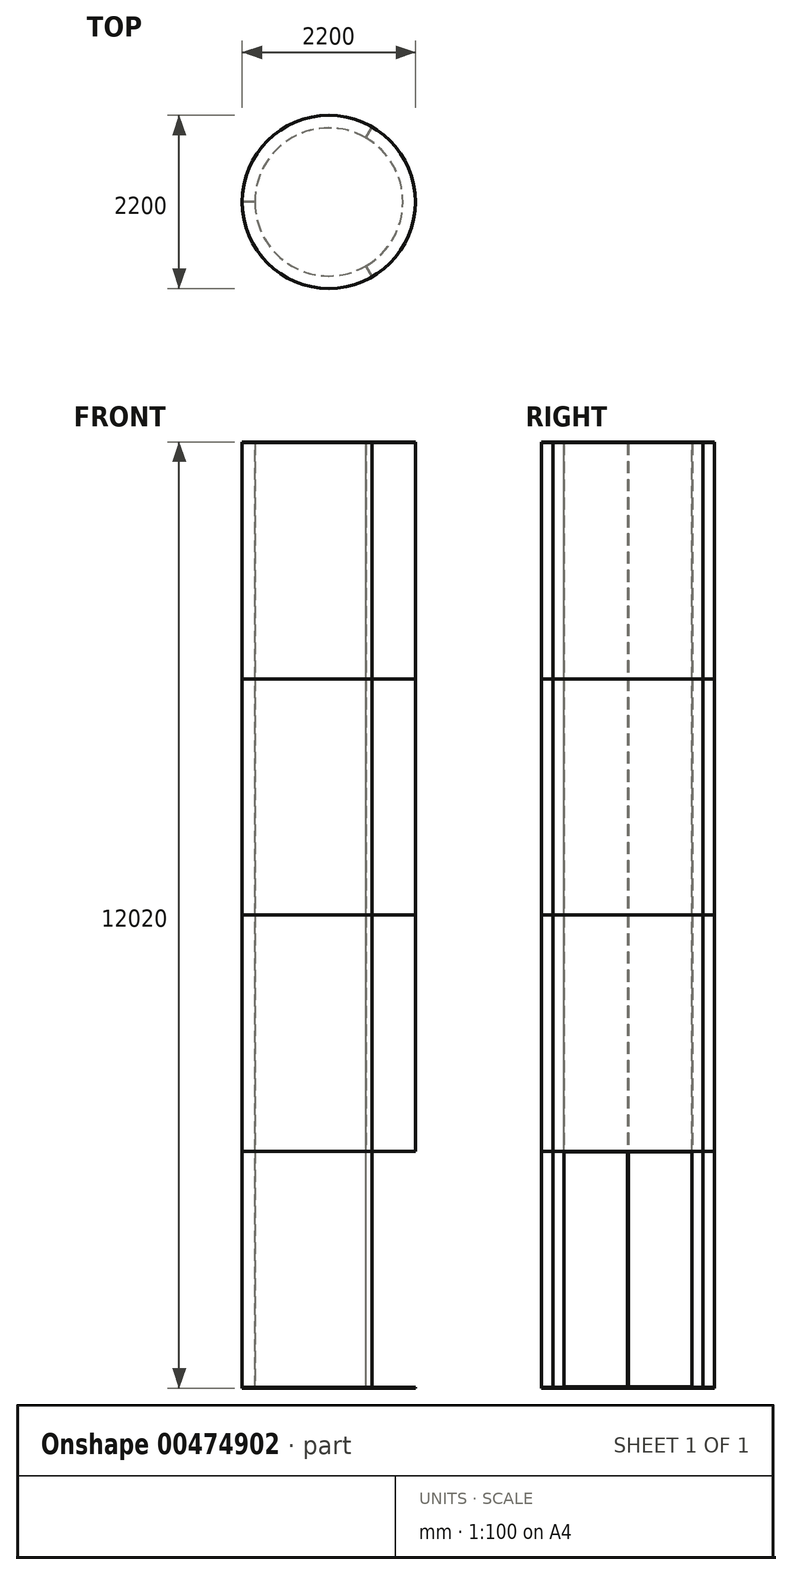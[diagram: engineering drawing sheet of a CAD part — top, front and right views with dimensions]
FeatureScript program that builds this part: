
annotation { "Feature Type Name" : "Feature", "Feature Type Description" : "" }
export const myFeature = defineFeature(function(context is Context, id is Id, definition is map)
    precondition{}
    {
        {
            var Q0;
            Q0=qCreatedBy(makeId("Front.planeOp"),FACE);
            var sketch = newSketch(context, id + "F0", { "sketchPlane" : qUnion([Q0])});
            skLineSegment(sketch, "E0", {"start": v(-940, 1500) * mm, "end": v(-1100, 1500) * mm});
            skLineSegment(sketch, "E1", {"start": v(-1100, 1500) * mm, "end": v(-1100, -1500) * mm});
            skLineSegment(sketch, "E2", {"start": v(-1100, -1500) * mm, "end": v(-940, -1500) * mm});
            skLineSegment(sketch, "E3.0", {"start": v(-1094, -1494) * mm, "end": v(-940, -1494) * mm});
            skLineSegment(sketch, "E3.1", {"start": v(-1094, 1494) * mm, "end": v(-1094, -1494) * mm});
            skLineSegment(sketch, "E3.2", {"start": v(-940, 1494) * mm, "end": v(-1094, 1494) * mm});
            skLineSegment(sketch, "E4", {"start": v(-940, 1494) * mm, "end": v(-940, 1500) * mm});
            skLineSegment(sketch, "E5", {"start": v(-940, -1500) * mm, "end": v(-940, -1494) * mm});
            skLineSegment(sketch, "E6", {"start": v(0, 0) * mm, "end": v(0, 1375.07) * mm, "construction": true});
            skSolve(sketch);
        }
        {
            var Q0;
            Q0 = qSketchRegion(id + "F0", true);
            var Q1;
            Q1=sQuery(id+"F0.wireOp",EDGE,"E6");
            revolve(context, id + "F1", {"entities" : qUnion([Q0]), "axis" : qUnion([Q1]), "revolveType" : RevolveType.TWO_DIRECTIONS, "angle" : 0 * degree, "angleBack" : 240 * degree});
        }
        {
            var Q0;
            Q0=makeQuery(id+"F1.opRevolve","SWEPT_FACE",FACE,{"disambiguationData":[OSD([sQuery(id+"F0.wireOp",EDGE,"E3.0")])]});
            var sketch = newSketch(context, id + "F2", { "sketchPlane" : qUnion([Q0])});
            skLineSegment(sketch, "E7", {"start": v(-940, 0) * mm, "end": v(-1094, 0) * mm});
            skLineSegment(sketch, "E8.0", {"start": v(-939.98, 6) * mm, "end": v(-1093.98, 6) * mm});
            skArc(sketch, "E9", {"start": v(-939.98, 6) * mm, "mid": v(-940, 3) * mm, "end": v(-940, 0) * mm});
            skArc(sketch, "E10", {"start": v(-1093.98, 6) * mm, "mid": v(-1094, 3) * mm, "end": v(-1094, 0) * mm});
            skLineSegment(sketch, "E11", {"start": v(470, 814.06) * mm, "end": v(547, 947.43) * mm});
            skLineSegment(sketch, "E12.0", {"start": v(464.8, 817.05) * mm, "end": v(541.8, 950.42) * mm});
            skArc(sketch, "E13", {"start": v(547, 947.43) * mm, "mid": v(544.4, 948.93) * mm, "end": v(541.8, 950.42) * mm});
            skArc(sketch, "E14", {"start": v(470, 814.06) * mm, "mid": v(467.4, 815.56) * mm, "end": v(464.8, 817.05) * mm});
            skSolve(sketch);
        }
        {
            var Q0;
            Q0=makeQuery(id+"F2.imprint","IMPRINT",FACE,{"disambiguationData":[TD([[makeQuery(id+"F2.imprint","IMPRINT",EDGE,{"derivedFrom":sQuery(id+"F2.wireOp",EDGE,"E7")}),1.0]])]});
            var Q1;
            Q1=makeQuery(id+"F2.imprint","IMPRINT",FACE,{"disambiguationData":[TD([[makeQuery(id+"F2.imprint","IMPRINT",EDGE,{"derivedFrom":sQuery(id+"F2.wireOp",EDGE,"E11")}),-1.0]])]});
            extrude(context, id + "F3", {"entities" : qUnion([Q0, Q1]), "operationType" : NewBodyOperationType.ADD, "depth" : (3000 - 12) * mm});
        }
        {
            var Q0;
            Q0=makeQuery(id+"F1.opRevolve","SWEPT_BODY",BODY,{"disambiguationData":[OSD([sQuery(id+"F0.wireOp",EDGE,"E0"),sQuery(id+"F0.wireOp",EDGE,"E1"),sQuery(id+"F0.wireOp",EDGE,"E2"),sQuery(id+"F0.wireOp",EDGE,"E3.0"),sQuery(id+"F0.wireOp",EDGE,"E3.1"),sQuery(id+"F0.wireOp",EDGE,"E3.2"),sQuery(id+"F0.wireOp",EDGE,"E4"),sQuery(id+"F0.wireOp",EDGE,"E5")])]});
            transform(context, id + "F4", {"entities" : qUnion([Q0]), "transformType" : TransformType.TRANSLATION_3D, "dx" : 0 * mm, "dy" : 0 * mm, "dz" : 3000 * mm, "makeCopy" : true});
        }
        {
            var Q0;
            Q0=makeQuery(id+"F4.opPattern","COPY",BODY,{"derivedFrom":makeQuery(id+"F1.opRevolve","SWEPT_BODY",BODY,{"disambiguationData":[OSD([sQuery(id+"F0.wireOp",EDGE,"E0"),sQuery(id+"F0.wireOp",EDGE,"E1"),sQuery(id+"F0.wireOp",EDGE,"E2"),sQuery(id+"F0.wireOp",EDGE,"E3.0"),sQuery(id+"F0.wireOp",EDGE,"E3.1"),sQuery(id+"F0.wireOp",EDGE,"E3.2"),sQuery(id+"F0.wireOp",EDGE,"E4"),sQuery(id+"F0.wireOp",EDGE,"E5")])]}),"instanceName":"1"});
            deleteBodies(context, id + "F5", {"entities" : qUnion([Q0])});
        }
        {
            var Q0;
            Q0=makeQuery(id+"F1.opRevolve","SWEPT_BODY",BODY,{"disambiguationData":[OSD([sQuery(id+"F0.wireOp",EDGE,"E0"),sQuery(id+"F0.wireOp",EDGE,"E1"),sQuery(id+"F0.wireOp",EDGE,"E2"),sQuery(id+"F0.wireOp",EDGE,"E3.0"),sQuery(id+"F0.wireOp",EDGE,"E3.1"),sQuery(id+"F0.wireOp",EDGE,"E3.2"),sQuery(id+"F0.wireOp",EDGE,"E4"),sQuery(id+"F0.wireOp",EDGE,"E5")])]});
            var Q1;
            Q1=sQuery(id+"F0.wireOp",EDGE,"E6");
            circularPattern(context, id + "F6", {"entities" : qUnion([Q0]), "axis" : qUnion([Q1]), "angle" : 120 * degree, "instanceCount" : 3, "equalSpace" : true, "isCentered" : true});
        }
        {
            var Q0;
            Q0=makeQuery(id+"F6.opPattern","COPY",BODY,{"derivedFrom":makeQuery(id+"F1.opRevolve","SWEPT_BODY",BODY,{"disambiguationData":[OSD([sQuery(id+"F0.wireOp",EDGE,"E0"),sQuery(id+"F0.wireOp",EDGE,"E1"),sQuery(id+"F0.wireOp",EDGE,"E2"),sQuery(id+"F0.wireOp",EDGE,"E3.0"),sQuery(id+"F0.wireOp",EDGE,"E3.1"),sQuery(id+"F0.wireOp",EDGE,"E3.2"),sQuery(id+"F0.wireOp",EDGE,"E4"),sQuery(id+"F0.wireOp",EDGE,"E5")])]}),"instanceName":"-2"});
            deleteBodies(context, id + "F7", {"entities" : qUnion([Q0])});
        }
        {
            var Q0;
            Q0=makeQuery(id+"F6.opPattern","COPY",BODY,{"derivedFrom":makeQuery(id+"F1.opRevolve","SWEPT_BODY",BODY,{"disambiguationData":[OSD([sQuery(id+"F0.wireOp",EDGE,"E0"),sQuery(id+"F0.wireOp",EDGE,"E1"),sQuery(id+"F0.wireOp",EDGE,"E2"),sQuery(id+"F0.wireOp",EDGE,"E3.0"),sQuery(id+"F0.wireOp",EDGE,"E3.1"),sQuery(id+"F0.wireOp",EDGE,"E3.2"),sQuery(id+"F0.wireOp",EDGE,"E4"),sQuery(id+"F0.wireOp",EDGE,"E5")])]}),"instanceName":"1"});
            deleteBodies(context, id + "F8", {"entities" : qUnion([Q0])});
        }
        {
            var Q0;
            Q0=makeQuery(id+"F6.opPattern","COPY",BODY,{"derivedFrom":makeQuery(id+"F1.opRevolve","SWEPT_BODY",BODY,{"disambiguationData":[OSD([sQuery(id+"F0.wireOp",EDGE,"E0"),sQuery(id+"F0.wireOp",EDGE,"E1"),sQuery(id+"F0.wireOp",EDGE,"E2"),sQuery(id+"F0.wireOp",EDGE,"E3.0"),sQuery(id+"F0.wireOp",EDGE,"E3.1"),sQuery(id+"F0.wireOp",EDGE,"E3.2"),sQuery(id+"F0.wireOp",EDGE,"E4"),sQuery(id+"F0.wireOp",EDGE,"E5")])]}),"instanceName":"-1"});
            deleteBodies(context, id + "F9", {"entities" : qUnion([Q0])});
        }
        {
            var Q0;
            Q0=makeQuery(id+"F1.opRevolve","SWEPT_BODY",BODY,{"disambiguationData":[OSD([sQuery(id+"F0.wireOp",EDGE,"E0"),sQuery(id+"F0.wireOp",EDGE,"E1"),sQuery(id+"F0.wireOp",EDGE,"E2"),sQuery(id+"F0.wireOp",EDGE,"E3.0"),sQuery(id+"F0.wireOp",EDGE,"E3.1"),sQuery(id+"F0.wireOp",EDGE,"E3.2"),sQuery(id+"F0.wireOp",EDGE,"E4"),sQuery(id+"F0.wireOp",EDGE,"E5")])]});
            transform(context, id + "F10", {"entities" : qUnion([Q0]), "transformType" : TransformType.TRANSLATION_3D, "dx" : 0 * mm, "dy" : 0 * mm, "dz" : 3000 * mm, "makeCopy" : true});
        }
        {
            var Q0;
            Q0=makeQuery(id+"F10.opPattern","COPY",BODY,{"derivedFrom":makeQuery(id+"F1.opRevolve","SWEPT_BODY",BODY,{"disambiguationData":[OSD([sQuery(id+"F0.wireOp",EDGE,"E0"),sQuery(id+"F0.wireOp",EDGE,"E1"),sQuery(id+"F0.wireOp",EDGE,"E2"),sQuery(id+"F0.wireOp",EDGE,"E3.0"),sQuery(id+"F0.wireOp",EDGE,"E3.1"),sQuery(id+"F0.wireOp",EDGE,"E3.2"),sQuery(id+"F0.wireOp",EDGE,"E4"),sQuery(id+"F0.wireOp",EDGE,"E5")])]}),"instanceName":"1"});
            transform(context, id + "F11", {"entities" : qUnion([Q0]), "transformType" : TransformType.TRANSLATION_3D, "dx" : 0 * mm, "dy" : 0 * mm, "dz" : 3000 * mm, "makeCopy" : true});
        }
        {
            var Q0;
            Q0=makeQuery(id+"F11.opPattern","COPY",BODY,{"derivedFrom":makeQuery(id+"F10.opPattern","COPY",BODY,{"derivedFrom":makeQuery(id+"F1.opRevolve","SWEPT_BODY",BODY,{"disambiguationData":[OSD([sQuery(id+"F0.wireOp",EDGE,"E0"),sQuery(id+"F0.wireOp",EDGE,"E1"),sQuery(id+"F0.wireOp",EDGE,"E2"),sQuery(id+"F0.wireOp",EDGE,"E3.0"),sQuery(id+"F0.wireOp",EDGE,"E3.1"),sQuery(id+"F0.wireOp",EDGE,"E3.2"),sQuery(id+"F0.wireOp",EDGE,"E4"),sQuery(id+"F0.wireOp",EDGE,"E5")])]}),"instanceName":"1"}),"instanceName":"1"});
            transform(context, id + "F12", {"entities" : qUnion([Q0]), "transformType" : TransformType.TRANSLATION_3D, "dx" : 0 * mm, "dy" : 0 * mm, "dz" : 3000 * mm, "makeCopy" : true});
        }
        {
            var Q0;
            Q0=makeQuery(id+"F12.opPattern","COPY",BODY,{"derivedFrom":makeQuery(id+"F11.opPattern","COPY",BODY,{"derivedFrom":makeQuery(id+"F10.opPattern","COPY",BODY,{"derivedFrom":makeQuery(id+"F1.opRevolve","SWEPT_BODY",BODY,{"disambiguationData":[OSD([sQuery(id+"F0.wireOp",EDGE,"E0"),sQuery(id+"F0.wireOp",EDGE,"E1"),sQuery(id+"F0.wireOp",EDGE,"E2"),sQuery(id+"F0.wireOp",EDGE,"E3.0"),sQuery(id+"F0.wireOp",EDGE,"E3.1"),sQuery(id+"F0.wireOp",EDGE,"E3.2"),sQuery(id+"F0.wireOp",EDGE,"E4"),sQuery(id+"F0.wireOp",EDGE,"E5")])]}),"instanceName":"1"}),"instanceName":"1"}),"instanceName":"1"});
            var Q1;
            Q1=makeQuery(id+"F11.opPattern","COPY",BODY,{"derivedFrom":makeQuery(id+"F10.opPattern","COPY",BODY,{"derivedFrom":makeQuery(id+"F1.opRevolve","SWEPT_BODY",BODY,{"disambiguationData":[OSD([sQuery(id+"F0.wireOp",EDGE,"E0"),sQuery(id+"F0.wireOp",EDGE,"E1"),sQuery(id+"F0.wireOp",EDGE,"E2"),sQuery(id+"F0.wireOp",EDGE,"E3.0"),sQuery(id+"F0.wireOp",EDGE,"E3.1"),sQuery(id+"F0.wireOp",EDGE,"E3.2"),sQuery(id+"F0.wireOp",EDGE,"E4"),sQuery(id+"F0.wireOp",EDGE,"E5")])]}),"instanceName":"1"}),"instanceName":"1"});
            var Q2;
            Q2=makeQuery(id+"F10.opPattern","COPY",BODY,{"derivedFrom":makeQuery(id+"F1.opRevolve","SWEPT_BODY",BODY,{"disambiguationData":[OSD([sQuery(id+"F0.wireOp",EDGE,"E0"),sQuery(id+"F0.wireOp",EDGE,"E1"),sQuery(id+"F0.wireOp",EDGE,"E2"),sQuery(id+"F0.wireOp",EDGE,"E3.0"),sQuery(id+"F0.wireOp",EDGE,"E3.1"),sQuery(id+"F0.wireOp",EDGE,"E3.2"),sQuery(id+"F0.wireOp",EDGE,"E4"),sQuery(id+"F0.wireOp",EDGE,"E5")])]}),"instanceName":"1"});
            var Q3;
            Q3=sQuery(id+"F0.wireOp",EDGE,"E6");
            circularPattern(context, id + "F13", {"entities" : qUnion([Q0, Q1, Q2]), "axis" : qUnion([Q3]), "angle" : 120 * degree, "instanceCount" : 2, "equalSpace" : true});
        }
        {
            var Q0;
            Q0=makeQuery(id+"F13.opPattern","COPY",BODY,{"derivedFrom":makeQuery(id+"F10.opPattern","COPY",BODY,{"derivedFrom":makeQuery(id+"F1.opRevolve","SWEPT_BODY",BODY,{"disambiguationData":[OSD([sQuery(id+"F0.wireOp",EDGE,"E0"),sQuery(id+"F0.wireOp",EDGE,"E1"),sQuery(id+"F0.wireOp",EDGE,"E2"),sQuery(id+"F0.wireOp",EDGE,"E3.0"),sQuery(id+"F0.wireOp",EDGE,"E3.1"),sQuery(id+"F0.wireOp",EDGE,"E3.2"),sQuery(id+"F0.wireOp",EDGE,"E4"),sQuery(id+"F0.wireOp",EDGE,"E5")])]}),"instanceName":"1"}),"instanceName":"1"});
            var Q1;
            Q1=makeQuery(id+"F13.opPattern","COPY",BODY,{"derivedFrom":makeQuery(id+"F11.opPattern","COPY",BODY,{"derivedFrom":makeQuery(id+"F10.opPattern","COPY",BODY,{"derivedFrom":makeQuery(id+"F1.opRevolve","SWEPT_BODY",BODY,{"disambiguationData":[OSD([sQuery(id+"F0.wireOp",EDGE,"E0"),sQuery(id+"F0.wireOp",EDGE,"E1"),sQuery(id+"F0.wireOp",EDGE,"E2"),sQuery(id+"F0.wireOp",EDGE,"E3.0"),sQuery(id+"F0.wireOp",EDGE,"E3.1"),sQuery(id+"F0.wireOp",EDGE,"E3.2"),sQuery(id+"F0.wireOp",EDGE,"E4"),sQuery(id+"F0.wireOp",EDGE,"E5")])]}),"instanceName":"1"}),"instanceName":"1"}),"instanceName":"1"});
            var Q2;
            Q2=makeQuery(id+"F13.opPattern","COPY",BODY,{"derivedFrom":makeQuery(id+"F12.opPattern","COPY",BODY,{"derivedFrom":makeQuery(id+"F11.opPattern","COPY",BODY,{"derivedFrom":makeQuery(id+"F10.opPattern","COPY",BODY,{"derivedFrom":makeQuery(id+"F1.opRevolve","SWEPT_BODY",BODY,{"disambiguationData":[OSD([sQuery(id+"F0.wireOp",EDGE,"E0"),sQuery(id+"F0.wireOp",EDGE,"E1"),sQuery(id+"F0.wireOp",EDGE,"E2"),sQuery(id+"F0.wireOp",EDGE,"E3.0"),sQuery(id+"F0.wireOp",EDGE,"E3.1"),sQuery(id+"F0.wireOp",EDGE,"E3.2"),sQuery(id+"F0.wireOp",EDGE,"E4"),sQuery(id+"F0.wireOp",EDGE,"E5")])]}),"instanceName":"1"}),"instanceName":"1"}),"instanceName":"1"}),"instanceName":"1"});
            var Q3;
            Q3=sQuery(id+"F0.wireOp",EDGE,"E6");
            circularPattern(context, id + "F14", {"entities" : qUnion([Q0, Q1, Q2]), "axis" : qUnion([Q3]), "angle" : 120 * degree, "instanceCount" : 2, "equalSpace" : true});
        }
        {
            var Q0;
            Q0=makeQuery(id+"F13.opPattern","COPY",FACE,{"derivedFrom":makeQuery(id+"F12.opPattern","COPY",FACE,{"derivedFrom":makeQuery(id+"F11.opPattern","COPY",FACE,{"derivedFrom":makeQuery(id+"F10.opPattern","COPY",FACE,{"derivedFrom":makeQuery(id+"F1.opRevolve","SWEPT_FACE",FACE,{"disambiguationData":[OSD([sQuery(id+"F0.wireOp",EDGE,"E0")])]}),"instanceName":"1"}),"instanceName":"1"}),"instanceName":"1"}),"instanceName":"1"});
            var sketch = newSketch(context, id + "F15", { "sketchPlane" : qUnion([Q0])});
            skCircle(sketch, "E15", {"center": v(0, 0) * mm, "radius": 1100 * mm});
            skSolve(sketch);
        }
        {
            var Q0;
            Q0 = qSketchRegion(id + "F15", true);
            extrude(context, id + "F16", {"entities" : qUnion([Q0]), "depth" : 10 * mm});
        }
        {
            var Q0;
            Q0=makeQuery(id+"F16.opExtrude","SWEPT_BODY",BODY,{"disambiguationData":[OSD([sQuery(id+"F15.wireOp",EDGE,"E15")])]});
            transform(context, id + "F17", {"entities" : qUnion([Q0]), "transformType" : TransformType.TRANSLATION_3D, "dx" : 0 * mm, "dy" : 0 * mm, "dz" : -12010 * mm, "makeCopy" : true});
        }
    });
